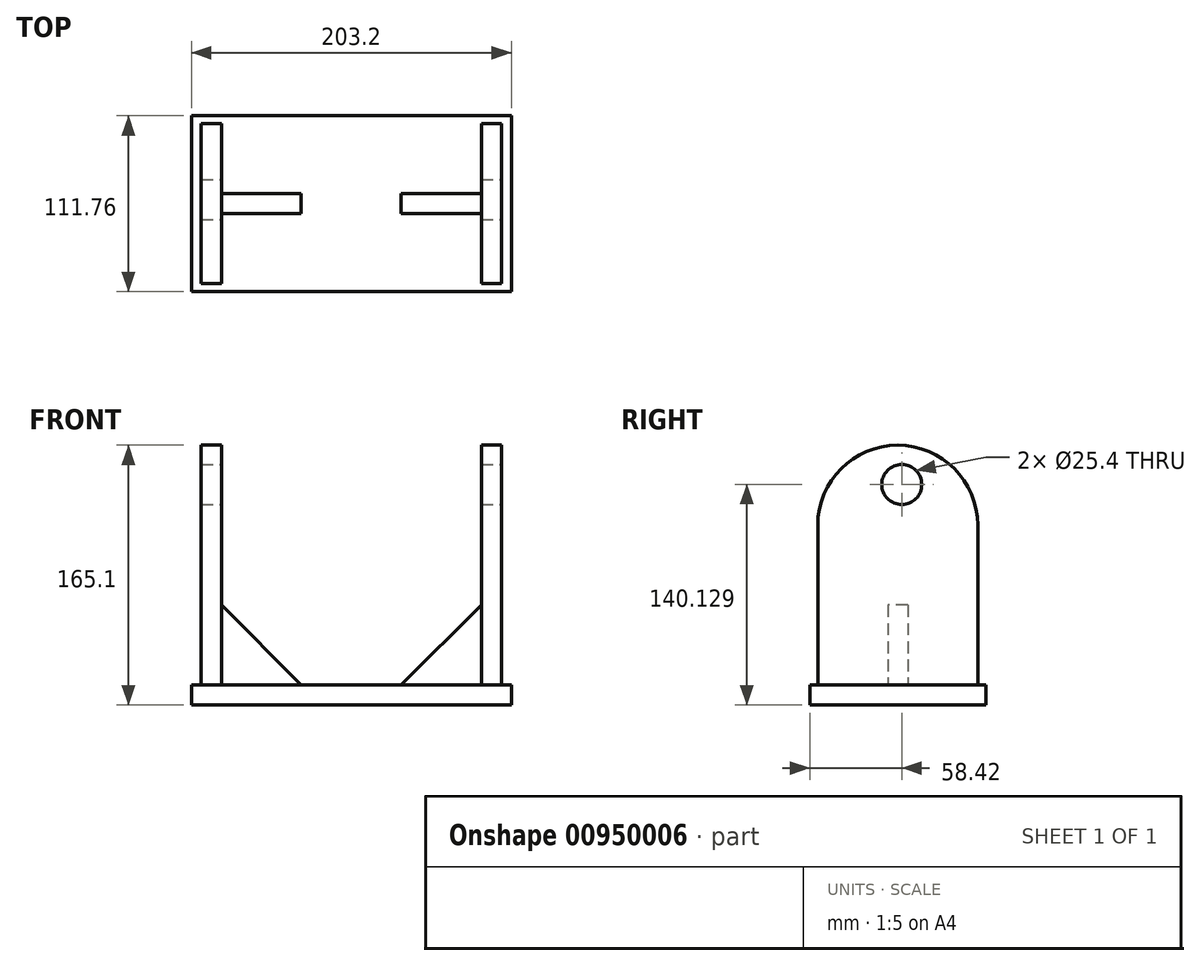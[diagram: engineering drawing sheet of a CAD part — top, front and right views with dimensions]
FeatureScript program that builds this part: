
annotation { "Feature Type Name" : "Feature", "Feature Type Description" : "" }
export const myFeature = defineFeature(function(context is Context, id is Id, definition is map)
    precondition{}
    {
        {
            var Q0;
            Q0=qCreatedBy(makeId("Top.planeOp"),FACE);
            var sketch = newSketch(context, id + "F0", { "sketchPlane" : qUnion([Q0])});
            skLineSegment(sketch, "E0.bottom", {"start": v(-101.6, 53.34) * mm, "end": v(101.6, 53.34) * mm});
            skLineSegment(sketch, "E0.top", {"start": v(-101.6, -58.42) * mm, "end": v(101.6, -58.42) * mm});
            skLineSegment(sketch, "E0.left", {"start": v(-101.6, 53.34) * mm, "end": v(-101.6, -58.42) * mm});
            skLineSegment(sketch, "E0.right", {"start": v(101.6, 53.34) * mm, "end": v(101.6, -58.42) * mm});
            skSolve(sketch);
        }
        {
            var Q0;
            Q0 = qSketchRegion(id + "F0", true);
            extrude(context, id + "F1", {"entities" : qUnion([Q0]), "depth" : 12.7 * mm, "offsetDistance" : 25.4 * mm});
        }
        {
            var Q0;
            Q0=makeQuery(id+"F1.opExtrude","CAP_FACE",FACE,{"disambiguationData":[OSD([sQuery(id+"F0.wireOp",EDGE,"E0.bottom"),sQuery(id+"F0.wireOp",EDGE,"E0.top"),sQuery(id+"F0.wireOp",EDGE,"E0.left"),sQuery(id+"F0.wireOp",EDGE,"E0.right")])],"isStart":false});
            var sketch = newSketch(context, id + "F2", { "sketchPlane" : qUnion([Q0])});
            skLineSegment(sketch, "E1.bottom", {"start": v(-95.25, 48.26) * mm, "end": v(-82.55, 48.26) * mm});
            skLineSegment(sketch, "E1.top", {"start": v(-95.25, -53.34) * mm, "end": v(-82.55, -53.34) * mm});
            skLineSegment(sketch, "E1.left", {"start": v(-95.25, 48.26) * mm, "end": v(-95.25, -53.34) * mm});
            skLineSegment(sketch, "E1.right", {"start": v(-82.55, 48.26) * mm, "end": v(-82.55, -53.34) * mm});
            skLineSegment(sketch, "E2.MirrorCS", {"start": v(95.25, 48.26) * mm, "end": v(95.25, -53.34) * mm});
            skLineSegment(sketch, "E3.MirrorCS", {"start": v(95.25, 48.26) * mm, "end": v(82.55, 48.26) * mm});
            skLineSegment(sketch, "E4.MirrorCS", {"start": v(82.55, 48.26) * mm, "end": v(82.55, -53.34) * mm});
            skLineSegment(sketch, "E5.MirrorCS", {"start": v(95.25, -53.34) * mm, "end": v(82.55, -53.34) * mm});
            skSolve(sketch);
        }
        {
            var Q0;
            Q0=makeQuery(id+"F2.imprint","IMPRINT",FACE,{"disambiguationData":[TD([[makeQuery(id+"F2.imprint","IMPRINT",EDGE,{"derivedFrom":sQuery(id+"F2.wireOp",EDGE,"E1.bottom")}),-1.0]])]});
            var Q1;
            Q1=makeQuery(id+"F2.imprint","IMPRINT",FACE,{"disambiguationData":[TD([[makeQuery(id+"F2.imprint","IMPRINT",EDGE,{"derivedFrom":sQuery(id+"F2.wireOp",EDGE,"E2.MirrorCS")}),-1.0]])]});
            extrude(context, id + "F3", {"entities" : qUnion([Q0, Q1]), "operationType" : NewBodyOperationType.ADD, "depth" : 152.4 * mm, "offsetDistance" : 25.4 * mm});
        }
        {
            var Q0;
            Q0=makeQuery(id+"F3.opExtrude","SWEPT_FACE",FACE,{"disambiguationData":[OSD([sQuery(id+"F2.wireOp",EDGE,"E2.MirrorCS")])]});
            var sketch = newSketch(context, id + "F4", { "sketchPlane" : qUnion([Q0])});
            skLineSegment(sketch, "E6", {"start": v(0, 140.13) * mm, "end": v(0, 165.1) * mm});
            skLineSegment(sketch, "E7", {"start": v(0, 140.13) * mm, "end": v(48.26, 140.13) * mm});
            skSolve(sketch);
        }
        {
            var Q0;
            Q0=sQuery(id+"F4.wireOp",VERTEX,"E6.start");
            var Q1;
            Q1=makeQuery(id+"F1.opExtrude","SWEPT_BODY",BODY,{"disambiguationData":[OSD([sQuery(id+"F0.wireOp",EDGE,"E0.bottom"),sQuery(id+"F0.wireOp",EDGE,"E0.top"),sQuery(id+"F0.wireOp",EDGE,"E0.left"),sQuery(id+"F0.wireOp",EDGE,"E0.right")])]});
            hole(context, id + "F5", {"style" : HoleStyle.SIMPLE, "endStyle" : HoleEndStyle.THROUGH, "holeDiameter" : 25.4 * mm, "majorDiameter" : 6.35 * mm, "isTappedThrough" : true, "tappedDepth" : 12.7 * mm, "tapClearance" : 3, "locations" : qUnion([Q0]), "scope" : qUnion([Q1])});
        }
        {
            var Q0;
            Q0=makeQuery(id+"F3.opExtrude","CAP_EDGE",EDGE,{"disambiguationData":[OSD([sQuery(id+"F2.wireOp",EDGE,"E1.top")])],"isStart":false});
            var Q1;
            Q1=makeQuery(id+"F3.opExtrude","CAP_EDGE",EDGE,{"disambiguationData":[OSD([sQuery(id+"F2.wireOp",EDGE,"E1.bottom")])],"isStart":false});
            fillet(context, id + "F6", {"entities" : qUnion([Q0, Q1]), "radius" : 50.8 * mm, "tangentPropagation" : true, "allowEdgeOverflow" : false});
        }
        {
            var Q0;
            Q0=makeQuery(id+"F3.opExtrude","CAP_EDGE",EDGE,{"disambiguationData":[OSD([sQuery(id+"F2.wireOp",EDGE,"E5.MirrorCS")])],"isStart":false});
            var Q1;
            Q1=makeQuery(id+"F3.opExtrude","CAP_EDGE",EDGE,{"disambiguationData":[OSD([sQuery(id+"F2.wireOp",EDGE,"E3.MirrorCS")])],"isStart":false});
            fillet(context, id + "F7", {"entities" : qUnion([Q0, Q1]), "radius" : 50.8 * mm, "tangentPropagation" : true, "allowEdgeOverflow" : false});
        }
        {
            var Q0;
            Q0=makeQuery(id+"F1.opExtrude","CAP_FACE",FACE,{"disambiguationData":[OSD([sQuery(id+"F0.wireOp",EDGE,"E0.bottom"),sQuery(id+"F0.wireOp",EDGE,"E0.top"),sQuery(id+"F0.wireOp",EDGE,"E0.left"),sQuery(id+"F0.wireOp",EDGE,"E0.right")])],"isStart":false});
            var sketch = newSketch(context, id + "F8", { "sketchPlane" : qUnion([Q0])});
            skLineSegment(sketch, "E8.bottom", {"start": v(-82.55, 3.8) * mm, "end": v(-31.75, 3.8) * mm});
            skLineSegment(sketch, "E8.top", {"start": v(-82.55, -8.9) * mm, "end": v(-31.75, -8.9) * mm});
            skLineSegment(sketch, "E8.left", {"start": v(-82.55, 3.8) * mm, "end": v(-82.55, -8.9) * mm});
            skLineSegment(sketch, "E8.right", {"start": v(-31.75, 3.8) * mm, "end": v(-31.75, -8.9) * mm});
            skLineSegment(sketch, "E9.MirrorCS", {"start": v(82.55, 3.8) * mm, "end": v(82.55, -8.9) * mm});
            skLineSegment(sketch, "E10.MirrorCS", {"start": v(82.55, -8.9) * mm, "end": v(31.75, -8.9) * mm});
            skLineSegment(sketch, "E11.MirrorCS", {"start": v(82.55, 3.8) * mm, "end": v(31.75, 3.8) * mm});
            skLineSegment(sketch, "E12.MirrorCS", {"start": v(31.75, 3.8) * mm, "end": v(31.75, -8.9) * mm});
            skSolve(sketch);
        }
        {
            var Q0;
            Q0=makeQuery(id+"F8.imprint","IMPRINT",FACE,{"disambiguationData":[TD([[makeQuery(id+"F8.imprint","IMPRINT",EDGE,{"derivedFrom":sQuery(id+"F8.wireOp",EDGE,"E8.bottom")}),-1.0]])]});
            var Q1;
            Q1=makeQuery(id+"F8.imprint","IMPRINT",FACE,{"disambiguationData":[TD([[makeQuery(id+"F8.imprint","IMPRINT",EDGE,{"derivedFrom":sQuery(id+"F8.wireOp",EDGE,"E9.MirrorCS")}),-1.0]])]});
            extrude(context, id + "F9", {"entities" : qUnion([Q0, Q1]), "operationType" : NewBodyOperationType.ADD, "depth" : 50.8 * mm, "offsetDistance" : 25.4 * mm});
        }
        {
            var Q0;
            Q0=makeQuery(id+"F9.opExtrude","CAP_EDGE",EDGE,{"disambiguationData":[OSD([sQuery(id+"FWPQuOQD1CP5tag_1.wireOp",EDGE,"uKp2VgZm-YiIM-U5j6-ICX9-Wn6LifjpMZkj.right")])],"isStart":false});
            var Q1;
            Q1=makeQuery(id+"F9.opExtrude","CAP_EDGE",EDGE,{"disambiguationData":[OSD([sQuery(id+"F8.wireOp",EDGE,"E8.right")])],"isStart":false});
            var Q2;
            Q2=makeQuery(id+"F9.opExtrude","CAP_EDGE",EDGE,{"disambiguationData":[OSD([sQuery(id+"F8.wireOp",EDGE,"E12.MirrorCS")])],"isStart":false});
            chamfer(context, id + "F10", {"entities" : qUnion([Q0, Q1, Q2]), "width" : 50.8 * mm, "tangentPropagation" : true});
        }
    });
